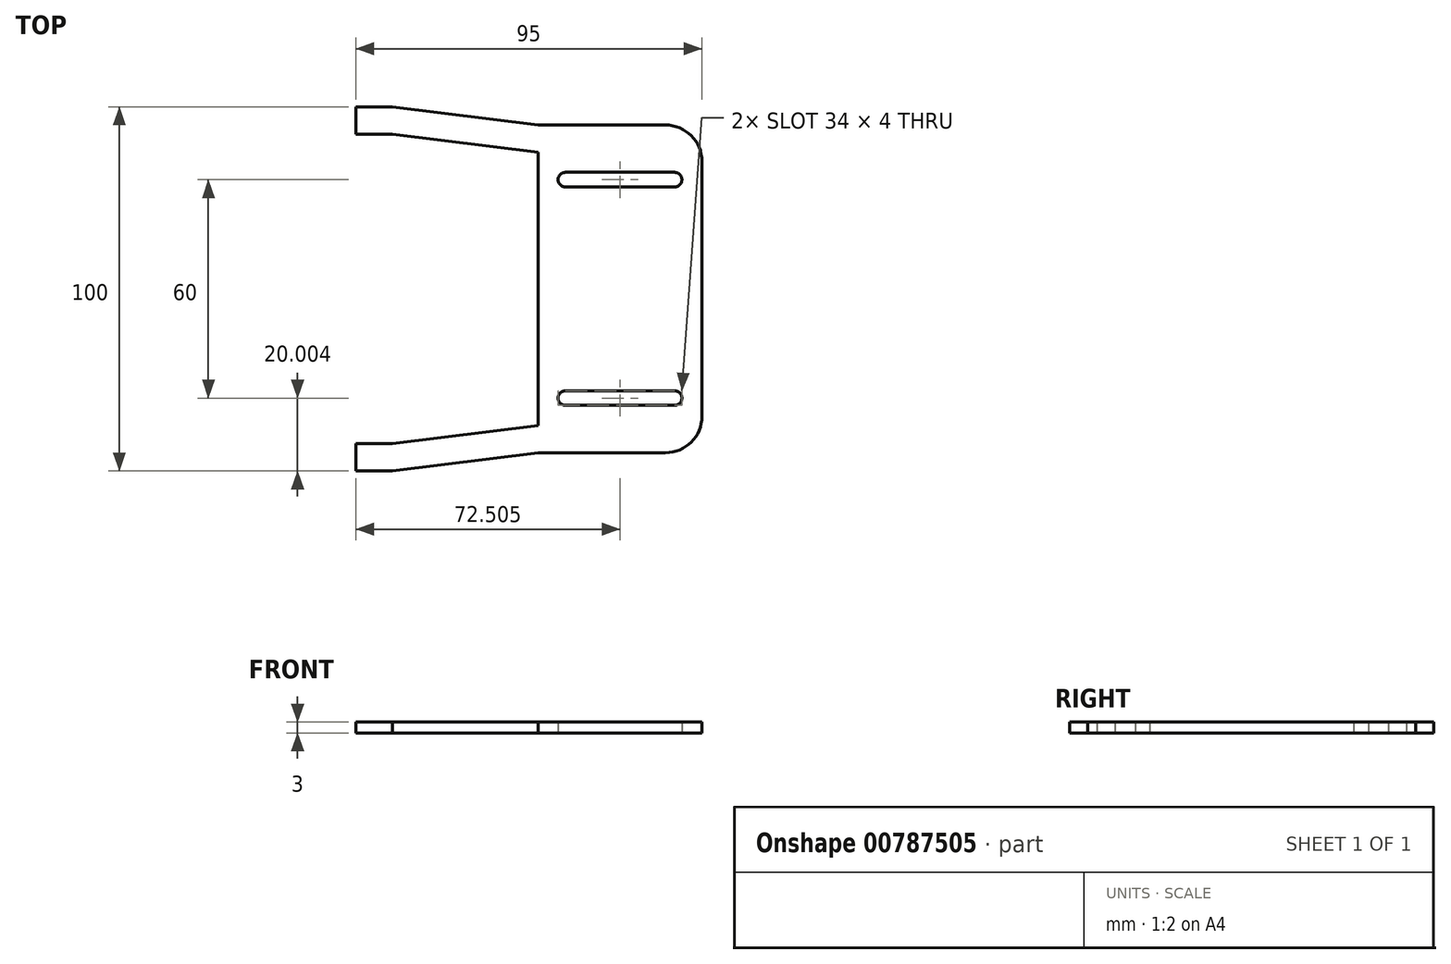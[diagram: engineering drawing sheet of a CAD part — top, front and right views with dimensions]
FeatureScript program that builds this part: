
annotation { "Feature Type Name" : "Feature", "Feature Type Description" : "" }
export const myFeature = defineFeature(function(context is Context, id is Id, definition is map)
    precondition{}
    {
        {
            var Q0;
            Q0=qCreatedBy(makeId("Top.planeOp"),FACE);
            var sketch = newSketch(context, id + "F0", { "sketchPlane" : qUnion([Q0])});
            skLineSegment(sketch, "E0.bottom", {"start": v(44.31, 46.21) * mm, "end": v(9.31, 46.21) * mm});
            skLineSegment(sketch, "E0.top", {"start": v(44.31, -43.79) * mm, "end": v(9.31, -43.79) * mm});
            skLineSegment(sketch, "E0.left", {"start": v(54.31, 36.21) * mm, "end": v(54.31, -33.79) * mm});
            skLineSegment(sketch, "E1.right", {"start": v(9.31, 38.71) * mm, "end": v(9.31, -36.29) * mm});
            skArc(sketch, "E2", {"start": v(46.81, 29.21) * mm, "mid": v(48.81, 31.21) * mm, "end": v(46.81, 33.21) * mm});
            skArc(sketch, "E3", {"start": v(16.81, 33.21) * mm, "mid": v(14.81, 31.21) * mm, "end": v(16.81, 29.21) * mm});
            skLineSegment(sketch, "E4", {"start": v(16.81, 33.21) * mm, "end": v(46.81, 33.21) * mm});
            skLineSegment(sketch, "E5", {"start": v(16.81, 29.21) * mm, "end": v(46.81, 29.21) * mm});
            skLineSegment(sketch, "E6", {"start": v(56.02, 1.21) * mm, "end": v(54.31, 1.21) * mm, "construction": true});
            skArc(sketch, "E7.MirrorCS", {"start": v(16.81, -30.79) * mm, "mid": v(14.81, -28.79) * mm, "end": v(16.81, -26.79) * mm});
            skArc(sketch, "E8.MirrorCS", {"start": v(46.81, -26.79) * mm, "mid": v(48.81, -28.79) * mm, "end": v(46.81, -30.79) * mm});
            skLineSegment(sketch, "E9.MirrorCS", {"start": v(16.81, -30.79) * mm, "end": v(46.81, -30.79) * mm});
            skLineSegment(sketch, "E10.MirrorCS", {"start": v(16.81, -26.79) * mm, "end": v(46.81, -26.79) * mm});
            skPoint(sketch, "E11.visualSharp", {"position": v(54.31, 46.21) * mm});
            skArc(sketch, "E11.filletArc", {"start": v(54.31, 36.21) * mm, "mid": v(51.39, 43.29) * mm, "end": v(44.31, 46.21) * mm});
            skPoint(sketch, "E12.visualSharp", {"position": v(54.31, -43.79) * mm});
            skArc(sketch, "E12.filletArc", {"start": v(44.31, -43.79) * mm, "mid": v(51.39, -40.86) * mm, "end": v(54.31, -33.79) * mm});
            skLineSegment(sketch, "E13", {"start": v(-40.69, 43.71) * mm, "end": v(-30.69, 43.71) * mm});
            skLineSegment(sketch, "E14", {"start": v(-30.69, 43.71) * mm, "end": v(9.31, 38.71) * mm});
            skLineSegment(sketch, "E15", {"start": v(9.31, 46.21) * mm, "end": v(-30.69, 51.21) * mm});
            skLineSegment(sketch, "E16", {"start": v(-40.69, -41.29) * mm, "end": v(-30.69, -41.29) * mm});
            skLineSegment(sketch, "E17", {"start": v(-30.69, -41.29) * mm, "end": v(9.31, -36.29) * mm});
            skLineSegment(sketch, "E18", {"start": v(9.31, -43.79) * mm, "end": v(-30.69, -48.79) * mm});
            skLineSegment(sketch, "E19", {"start": v(-40.69, -41.29) * mm, "end": v(-40.69, -48.79) * mm});
            skLineSegment(sketch, "E20", {"start": v(-40.69, 43.71) * mm, "end": v(-40.69, 51.21) * mm});
            skLineSegment(sketch, "E21", {"start": v(-30.69, -48.79) * mm, "end": v(-40.69, -48.79) * mm});
            skLineSegment(sketch, "E22", {"start": v(-30.69, 51.21) * mm, "end": v(-40.69, 51.21) * mm});
            skSolve(sketch);
        }
        {
            var Q0;
            Q0=makeQuery(id+"F0.imprint","IMPRINT",FACE,{"disambiguationData":[TD([[makeQuery(id+"F0.imprint","IMPRINT",EDGE,{"derivedFrom":sQuery(id+"F0.wireOp",EDGE,"E0.bottom")}),1.0]])]});
            extrude(context, id + "F1", {"entities" : qUnion([Q0]), "depth" : 3 * mm, "offsetDistance" : 25.4 * mm});
        }
    });
